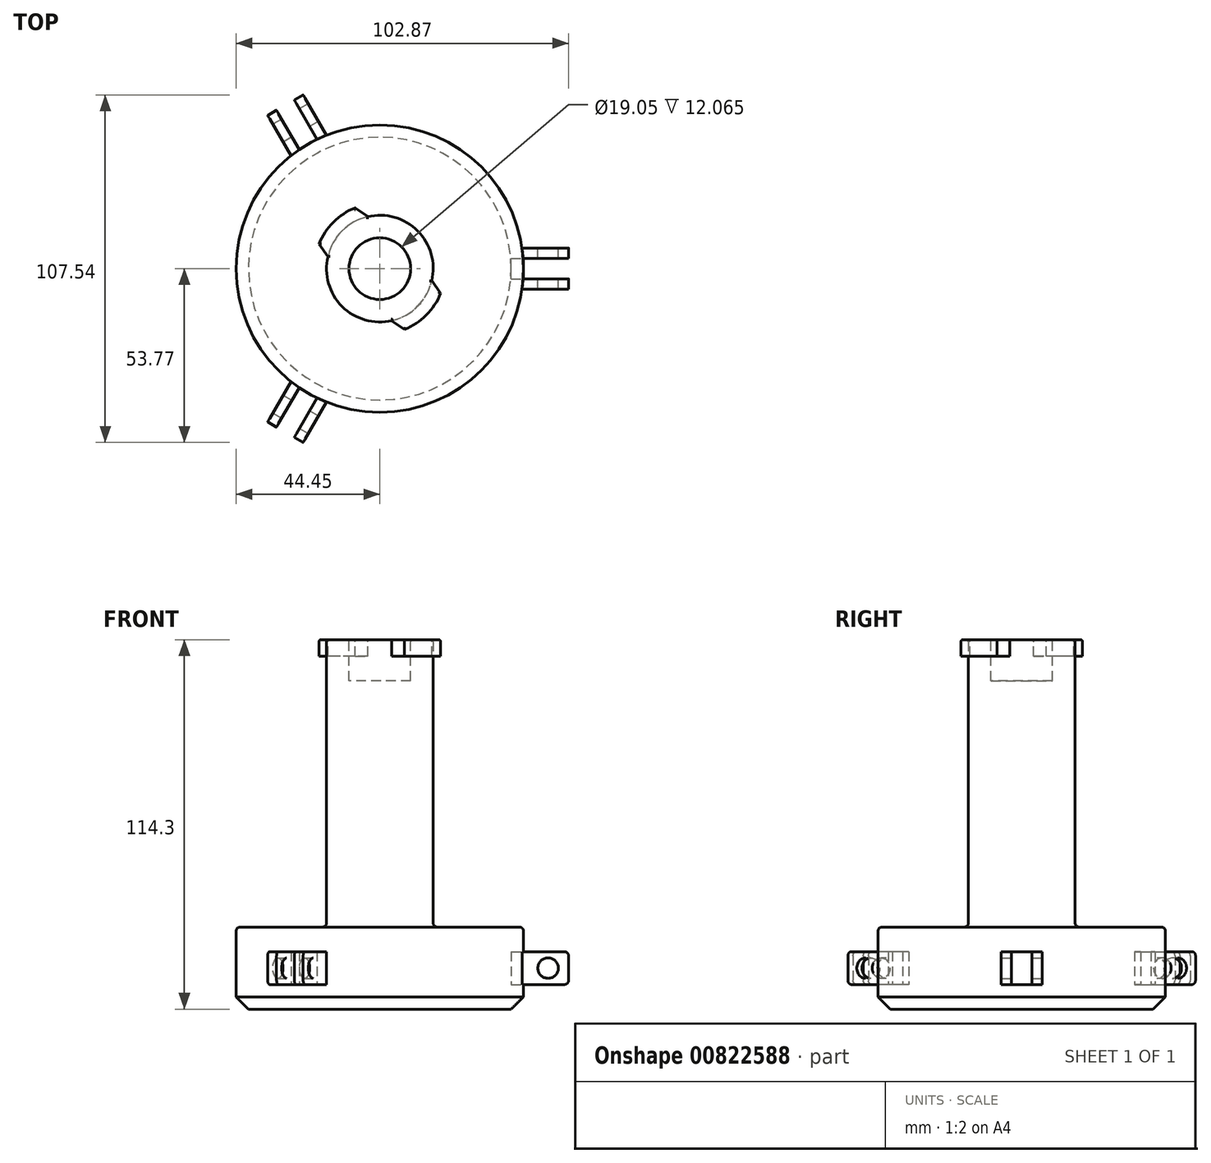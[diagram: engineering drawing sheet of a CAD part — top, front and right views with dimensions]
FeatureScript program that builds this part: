
annotation { "Feature Type Name" : "Feature", "Feature Type Description" : "" }
export const myFeature = defineFeature(function(context is Context, id is Id, definition is map)
    precondition{}
    {
        {
            var Q0;
            Q0=qCreatedBy(makeId("Top.planeOp"),FACE);
            var sketch = newSketch(context, id + "F0", { "sketchPlane" : qUnion([Q0])});
            skCircle(sketch, "E0", {"center": v(0, 0) * mm, "radius": 44.45 * mm});
            skCircle(sketch, "E1", {"center": v(0, 0) * mm, "radius": 16.51 * mm});
            skSolve(sketch);
        }
        {
            var Q0;
            Q0=makeQuery(id+"F0.imprint","IMPRINT",FACE,{"disambiguationData":[TD([[makeQuery(id+"F0.imprint","IMPRINT",EDGE,{"derivedFrom":sQuery(id+"F0.wireOp",EDGE,"E0")}),1.0]])]});
            var Q1;
            Q1=makeQuery(id+"F0.imprint","IMPRINT",FACE,{"disambiguationData":[TD([[makeQuery(id+"F0.imprint","IMPRINT",EDGE,{"derivedFrom":sQuery(id+"F0.wireOp",EDGE,"E1")}),1.0]])]});
            extrude(context, id + "F1", {"entities" : qUnion([Q0, Q1]), "depth" : 25.4 * mm, "offsetDistance" : 25.4 * mm});
        }
        {
            var Q0;
            Q0=makeQuery(id+"F0.imprint","IMPRINT",FACE,{"disambiguationData":[TD([[makeQuery(id+"F0.imprint","IMPRINT",EDGE,{"derivedFrom":sQuery(id+"F0.wireOp",EDGE,"E1")}),1.0]])]});
            extrude(context, id + "F2", {"entities" : qUnion([Q0]), "operationType" : NewBodyOperationType.ADD, "depth" : 114.3 * mm, "offsetDistance" : 25.4 * mm});
        }
        {
            var Q0;
            Q0=qCreatedBy(makeId("Front.planeOp"),FACE);
            var sketch = newSketch(context, id + "F3", { "sketchPlane" : qUnion([Q0])});
            skLineSegment(sketch, "E2.bottom", {"start": v(40.64, 17.78) * mm, "end": v(57.15, 17.78) * mm});
            skLineSegment(sketch, "E2.top", {"start": v(40.64, 7.62) * mm, "end": v(57.15, 7.62) * mm});
            skLineSegment(sketch, "E2.left", {"start": v(40.64, 17.78) * mm, "end": v(40.64, 7.62) * mm});
            skLineSegment(sketch, "E2.right", {"start": v(58.42, 16.51) * mm, "end": v(58.42, 8.9) * mm});
            skPoint(sketch, "E3.visualSharp", {"position": v(58.42, 17.78) * mm});
            skArc(sketch, "E3.filletArc", {"start": v(58.42, 16.51) * mm, "mid": v(58.05, 17.4) * mm, "end": v(57.15, 17.78) * mm});
            skPoint(sketch, "E4.visualSharp", {"position": v(58.42, 7.62) * mm});
            skArc(sketch, "E4.filletArc", {"start": v(57.15, 7.62) * mm, "mid": v(58.05, 8) * mm, "end": v(58.42, 8.9) * mm});
            skCircle(sketch, "E5", {"center": v(52.07, 12.7) * mm, "radius": 3.18 * mm});
            skSolve(sketch);
        }
        {
            var Q0;
            Q0 = qSketchRegion(id + "F3", true);
            extrude(context, id + "F4", {"entities" : qUnion([Q0]), "endBound" : BoundingType.SYMMETRIC, "depth" : 12.7 * mm, "offsetDistance" : 25.4 * mm});
        }
        {
            var Q0;
            Q0 = qSketchRegion(id + "F3", true);
            extrude(context, id + "F5", {"entities" : qUnion([Q0]), "operationType" : NewBodyOperationType.REMOVE, "endBound" : BoundingType.SYMMETRIC, "depth" : 6.35 * mm, "offsetDistance" : 25.4 * mm});
        }
        {
            var Q0;
            Q0=makeQuery(id+"F1.opExtrude","CAP_FACE",FACE,{"disambiguationData":[OSD([sQuery(id+"F0.wireOp",EDGE,"E0")])],"isStart":false});
            fillet(context, id + "F6", {"entities" : qUnion([Q0]), "radius" : 1.27 * mm, "tangentPropagation" : true, "allowEdgeOverflow" : false});
        }
        {
            var Q0;
            Q0=makeQuery(id+"F1.opExtrude","CAP_EDGE",EDGE,{"disambiguationData":[OSD([sQuery(id+"F0.wireOp",EDGE,"E0")])],"isStart":true});
            chamfer(context, id + "F7", {"entities" : qUnion([Q0]), "width" : 3.8 * mm, "tangentPropagation" : true});
        }
        {
            var Q0;
            Q0=makeQuery(id+"F5.boolean.opBoolean","SPLIT",BODY,{"disambiguationData":[OD(1.0)],"derivedFrom":makeQuery(id+"F4.opExtrude","SWEPT_BODY",BODY,{"disambiguationData":[OSD([sQuery(id+"F3.wireOp",EDGE,"E2.bottom"),sQuery(id+"F3.wireOp",EDGE,"E2.top"),sQuery(id+"F3.wireOp",EDGE,"E2.left"),sQuery(id+"F3.wireOp",EDGE,"E2.right"),sQuery(id+"F3.wireOp",EDGE,"E3.filletArc"),sQuery(id+"F3.wireOp",EDGE,"E4.filletArc"),sQuery(id+"F3.wireOp",EDGE,"E5")])]})});
            var Q1;
            Q1=makeQuery(id+"F5.boolean.opBoolean","SPLIT",BODY,{"disambiguationData":[OD(0.0)],"derivedFrom":makeQuery(id+"F4.opExtrude","SWEPT_BODY",BODY,{"disambiguationData":[OSD([sQuery(id+"F3.wireOp",EDGE,"E2.bottom"),sQuery(id+"F3.wireOp",EDGE,"E2.top"),sQuery(id+"F3.wireOp",EDGE,"E2.left"),sQuery(id+"F3.wireOp",EDGE,"E2.right"),sQuery(id+"F3.wireOp",EDGE,"E3.filletArc"),sQuery(id+"F3.wireOp",EDGE,"E4.filletArc"),sQuery(id+"F3.wireOp",EDGE,"E5")])]})});
            var Q2;
            Q2=makeQuery(id+"F1.opExtrude","SWEPT_FACE",FACE,{"disambiguationData":[OSD([sQuery(id+"F0.wireOp",EDGE,"E0")])]});
            circularPattern(context, id + "F8", {"operationType" : NewBodyOperationType.ADD, "entities" : qUnion([Q0, Q1]), "axis" : qUnion([Q2]), "angle" : 360 * degree, "instanceCount" : 3, "equalSpace" : true, "isCentered" : true});
        }
        {
            var Q0;
            Q0=makeQuery(id+"F2.opExtrude","CAP_FACE",FACE,{"disambiguationData":[OSD([sQuery(id+"F0.wireOp",EDGE,"E1")])],"isStart":false});
            var sketch = newSketch(context, id + "F9", { "sketchPlane" : qUnion([Q0])});
            skCircle(sketch, "E6", {"center": v(0, 0) * mm, "radius": 16.51 * mm});
            skCircle(sketch, "E7", {"center": v(0, 0) * mm, "radius": 20.32 * mm});
            skCircle(sketch, "E8", {"center": v(0, 0) * mm, "radius": 17.78 * mm, "construction": true});
            skLineSegment(sketch, "E9", {"start": v(-5.08, 17.04) * mm, "end": v(-7.62, 18.84) * mm});
            skLineSegment(sketch, "E10", {"start": v(-17.04, 5.08) * mm, "end": v(-18.84, 7.62) * mm});
            skLineSegment(sketch, "E11", {"start": v(-14.37, 14.37) * mm, "end": v(0, 0) * mm, "construction": true});
            skLineSegment(sketch, "E12", {"start": v(-11.67, -11.67) * mm, "end": v(0, 0) * mm, "construction": true});
            skLineSegment(sketch, "E13", {"start": v(0, 0) * mm, "end": v(11.67, 11.67) * mm, "construction": true});
            skLineSegment(sketch, "E14", {"start": v(-14.37, 14.37) * mm, "end": v(-7.62, 18.84) * mm, "construction": true});
            skLineSegment(sketch, "E15", {"start": v(-14.37, 14.37) * mm, "end": v(-18.84, 7.62) * mm, "construction": true});
            skLineSegment(sketch, "E16.MirrorCS", {"start": v(5.08, -17.04) * mm, "end": v(7.62, -18.84) * mm});
            skLineSegment(sketch, "E17.MirrorCS", {"start": v(17.04, -5.08) * mm, "end": v(18.84, -7.62) * mm});
            skLineSegment(sketch, "E18", {"start": v(-17.04, 5.08) * mm, "end": v(-16.08, 3.73) * mm});
            skLineSegment(sketch, "E19", {"start": v(-5.08, 17.04) * mm, "end": v(-3.73, 16.08) * mm});
            skLineSegment(sketch, "E20.MirrorCS", {"start": v(17.04, -5.08) * mm, "end": v(16.08, -3.73) * mm});
            skLineSegment(sketch, "E21.MirrorCS", {"start": v(5.08, -17.04) * mm, "end": v(3.73, -16.08) * mm});
            skSolve(sketch);
        }
        {
            var Q0;
            {var subQ0=sQuery(id+"F9.wireOp",EDGE,"E9");Q0=makeQuery(id+"F9.imprint","IMPRINT",FACE,{"disambiguationData":[TD([[makeQuery(id+"F9.imprint","IMPRINT",EDGE,{"derivedFrom":subQ0}),1.0]])]});}
            var Q1;
            {var subQ0=sQuery(id+"F9.wireOp",EDGE,"E16.MirrorCS");Q1=makeQuery(id+"F9.imprint","IMPRINT",FACE,{"disambiguationData":[TD([[makeQuery(id+"F9.imprint","IMPRINT",EDGE,{"derivedFrom":subQ0}),1.0]])]});}
            extrude(context, id + "F10", {"entities" : qUnion([Q0, Q1]), "operationType" : NewBodyOperationType.ADD, "oppositeDirection" : true, "depth" : 5.08 * mm, "offsetDistance" : 25.4 * mm});
        }
        {
            var Q0;
            {var subQ0=sQuery(id+"F9.wireOp",EDGE,"E7");var subQ1=sQuery(id+"F9.wireOp",EDGE,"E6");Q0=makeQuery(id+"F10.boolean.opBoolean","MERGE",FACE,{"derivedFrom":[makeQuery(id+"F2.opExtrude","CAP_FACE",FACE,{"disambiguationData":[OSD([sQuery(id+"F0.wireOp",EDGE,"E1")])],"isStart":false}),makeQuery(id+"F10.opExtrude","CAP_FACE",FACE,{"disambiguationData":[OSD([subQ1,subQ0,sQuery(id+"F9.wireOp",EDGE,"E9"),sQuery(id+"F9.wireOp",EDGE,"E10"),sQuery(id+"F9.wireOp",EDGE,"E18"),sQuery(id+"F9.wireOp",EDGE,"E19")])],"isStart":true}),makeQuery(id+"F10.opExtrude","CAP_FACE",FACE,{"disambiguationData":[OSD([subQ1,subQ0,sQuery(id+"F9.wireOp",EDGE,"E16.MirrorCS"),sQuery(id+"F9.wireOp",EDGE,"E17.MirrorCS"),sQuery(id+"F9.wireOp",EDGE,"E20.MirrorCS"),sQuery(id+"F9.wireOp",EDGE,"E21.MirrorCS")])],"isStart":true})]});}
            var sketch = newSketch(context, id + "F11", { "sketchPlane" : qUnion([Q0])});
            skCircle(sketch, "E22", {"center": v(0, 0) * mm, "radius": 9.53 * mm});
            skSolve(sketch);
        }
        {
            var Q0;
            Q0 = qSketchRegion(id + "F11", true);
            extrude(context, id + "F12", {"entities" : qUnion([Q0]), "operationType" : NewBodyOperationType.REMOVE, "oppositeDirection" : true, "depth" : 12.7 * mm, "offsetDistance" : 25.4 * mm});
        }
        {
            var Q0;
            {var subQ0=sQuery(id+"F9.wireOp",EDGE,"E7");var subQ1=sQuery(id+"F9.wireOp",EDGE,"E6");Q0=makeQuery(id+"F10.boolean.opBoolean","MERGE",FACE,{"derivedFrom":[makeQuery(id+"F2.opExtrude","CAP_FACE",FACE,{"disambiguationData":[OSD([sQuery(id+"F0.wireOp",EDGE,"E1")])],"isStart":false}),makeQuery(id+"F10.opExtrude","CAP_FACE",FACE,{"disambiguationData":[OSD([subQ1,subQ0,sQuery(id+"F9.wireOp",EDGE,"E9"),sQuery(id+"F9.wireOp",EDGE,"E10"),sQuery(id+"F9.wireOp",EDGE,"E18"),sQuery(id+"F9.wireOp",EDGE,"E19")])],"isStart":true}),makeQuery(id+"F10.opExtrude","CAP_FACE",FACE,{"disambiguationData":[OSD([subQ1,subQ0,sQuery(id+"F9.wireOp",EDGE,"E16.MirrorCS"),sQuery(id+"F9.wireOp",EDGE,"E17.MirrorCS"),sQuery(id+"F9.wireOp",EDGE,"E20.MirrorCS"),sQuery(id+"F9.wireOp",EDGE,"E21.MirrorCS")])],"isStart":true})]});}
            fillet(context, id + "F13", {"entities" : qUnion([Q0]), "tangentPropagation" : true, "radius" : 0.64 * mm, "defaultsChanged" : true, "vertexSettings" : [], "allowEdgeOverflow" : false});
        }
    });
